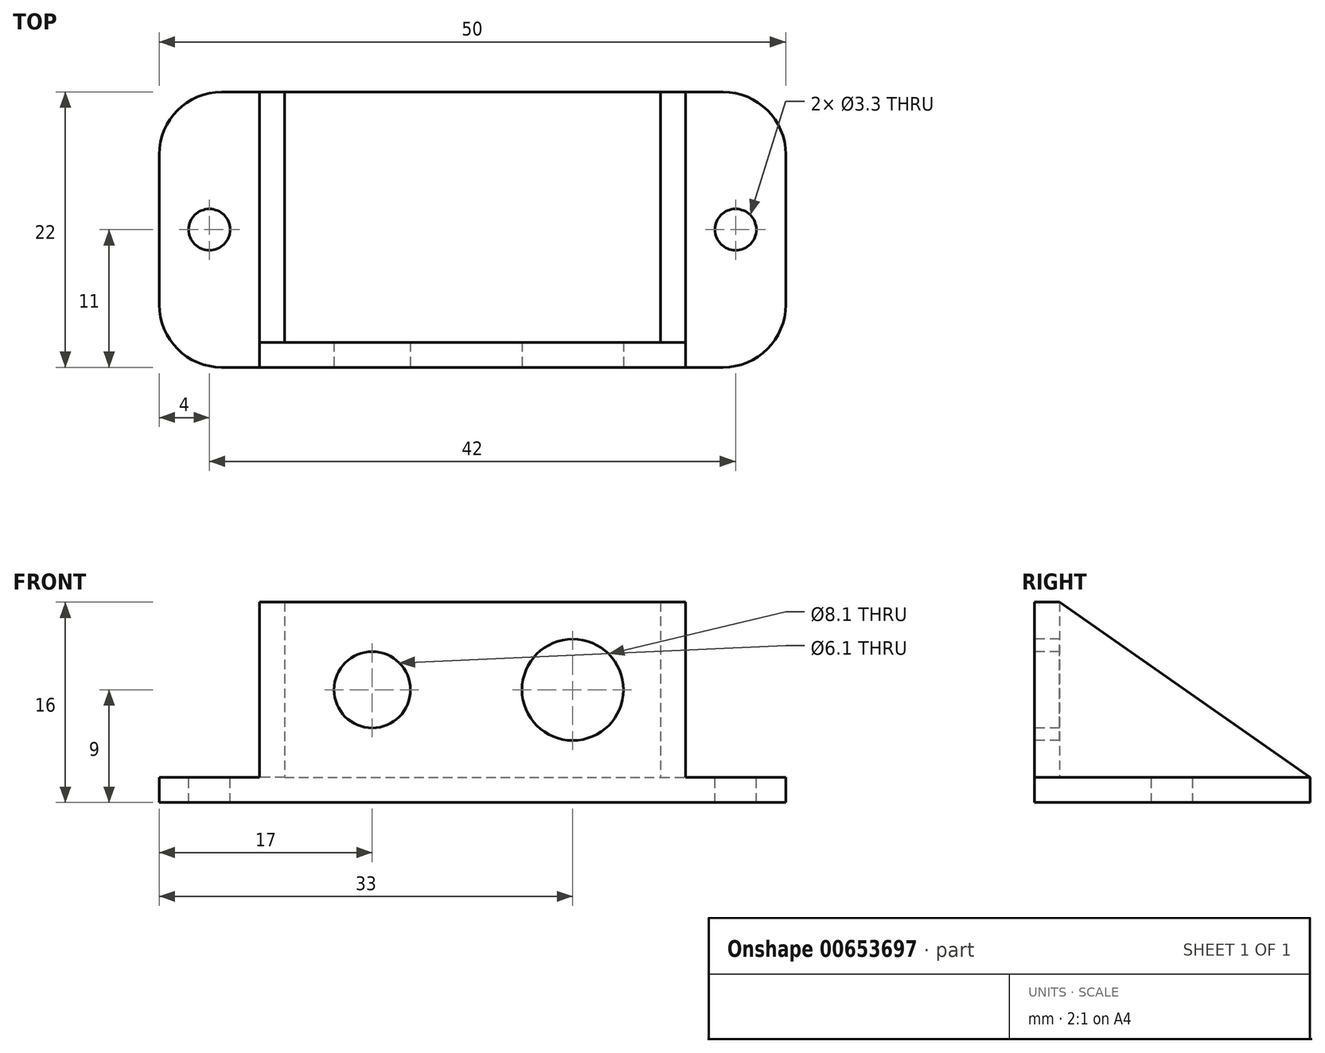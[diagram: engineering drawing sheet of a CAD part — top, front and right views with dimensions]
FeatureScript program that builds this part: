
annotation { "Feature Type Name" : "Feature", "Feature Type Description" : "" }
export const myFeature = defineFeature(function(context is Context, id is Id, definition is map)
    precondition{}
    {
        {
            var Q0;
            Q0=qCreatedBy(makeId("Top.planeOp"),FACE);
            var sketch = newSketch(context, id + "F0", { "sketchPlane" : qUnion([Q0])});
            skLineSegment(sketch, "E0.bottom", {"start": v(-25, 11) * mm, "end": v(25, 11) * mm});
            skLineSegment(sketch, "E0.top", {"start": v(-25, -11) * mm, "end": v(25, -11) * mm});
            skLineSegment(sketch, "E0.left", {"start": v(-25, 11) * mm, "end": v(-25, -11) * mm});
            skLineSegment(sketch, "E0.right", {"start": v(25, 11) * mm, "end": v(25, -11) * mm});
            skPoint(sketch, "E0.middle", {"position": v(0, 0) * mm});
            skSolve(sketch);
        }
        {
            var Q0;
            Q0=makeQuery(id+"F0.imprint","IMPRINT",FACE,{"disambiguationData":[TD([[makeQuery(id+"F0.imprint","IMPRINT",EDGE,{"derivedFrom":sQuery(id+"F0.wireOp",EDGE,"E0.bottom")}),-1.0]])]});
            extrude(context, id + "F1", {"entities" : qUnion([Q0]), "depth" : 2 * mm, "offsetDistance" : 25 * mm});
        }
        {
            var Q0;
            Q0=makeQuery(id+"F1.opExtrude","CAP_FACE",FACE,{"disambiguationData":[OSD([sQuery(id+"F0.wireOp",EDGE,"E0.bottom"),sQuery(id+"F0.wireOp",EDGE,"E0.top"),sQuery(id+"F0.wireOp",EDGE,"E0.left"),sQuery(id+"F0.wireOp",EDGE,"E0.right")])],"isStart":false});
            var sketch = newSketch(context, id + "F2", { "sketchPlane" : qUnion([Q0])});
            skLineSegment(sketch, "E1.bottom", {"start": v(17, -11) * mm, "end": v(-17, -11) * mm});
            skLineSegment(sketch, "E1.top", {"start": v(17, -9) * mm, "end": v(-17, -9) * mm});
            skLineSegment(sketch, "E1.left", {"start": v(17, -11) * mm, "end": v(17, -9) * mm});
            skLineSegment(sketch, "E1.right", {"start": v(-17, -11) * mm, "end": v(-17, -9) * mm});
            skPoint(sketch, "E1.middle", {"position": v(0, -10) * mm});
            skPoint(sketch, "E1.middle.positionSnap0", {"position": v(0, -11) * mm});
            skPoint(sketch, "E1.centerSnap0", {"position": v(0, -11) * mm});
            skSolve(sketch);
        }
        {
            var Q0;
            Q0=makeQuery(id+"F2.imprint","IMPRINT",FACE,{"disambiguationData":[TD([[makeQuery(id+"F2.imprint","IMPRINT",EDGE,{"derivedFrom":sQuery(id+"F2.wireOp",EDGE,"E1.bottom")}),1.0]])]});
            extrude(context, id + "F3", {"entities" : qUnion([Q0]), "operationType" : NewBodyOperationType.ADD, "depth" : 14 * mm, "offsetDistance" : 25 * mm});
        }
        {
            var Q0;
            Q0=makeQuery(id+"F3.boolean.opBoolean","MERGE",FACE,{"derivedFrom":[makeQuery(id+"F1.opExtrude","SWEPT_FACE",FACE,{"disambiguationData":[OSD([sQuery(id+"F0.wireOp",EDGE,"E0.top")])]}),makeQuery(id+"F3.opExtrude","SWEPT_FACE",FACE,{"disambiguationData":[OSD([sQuery(id+"F2.wireOp",EDGE,"E1.bottom")])]})]});
            var sketch = newSketch(context, id + "F4", { "sketchPlane" : qUnion([Q0])});
            skCircle(sketch, "E2", {"center": v(-8, 9) * mm, "radius": 3.05 * mm});
            skCircle(sketch, "E3", {"center": v(8, 9) * mm, "radius": 4.05 * mm});
            skSolve(sketch);
        }
        {
            var Q0;
            Q0 = qSketchRegion(id + "F4", true);
            extrude(context, id + "F5", {"entities" : qUnion([Q0]), "operationType" : NewBodyOperationType.REMOVE, "oppositeDirection" : true, "depth" : 2 * mm, "offsetDistance" : 25 * mm});
        }
        {
            var Q0;
            Q0=makeQuery(id+"F1.opExtrude","CAP_FACE",FACE,{"disambiguationData":[OSD([sQuery(id+"F0.wireOp",EDGE,"E0.bottom"),sQuery(id+"F0.wireOp",EDGE,"E0.top"),sQuery(id+"F0.wireOp",EDGE,"E0.left"),sQuery(id+"F0.wireOp",EDGE,"E0.right")])],"isStart":false});
            var sketch = newSketch(context, id + "F6", { "sketchPlane" : qUnion([Q0])});
            skCircle(sketch, "E4", {"center": v(-21, 0) * mm, "radius": 1.65 * mm});
            skCircle(sketch, "E5", {"center": v(21, 0) * mm, "radius": 1.65 * mm});
            skSolve(sketch);
        }
        {
            var Q0;
            Q0 = qSketchRegion(id + "F6", true);
            extrude(context, id + "F7", {"entities" : qUnion([Q0]), "operationType" : NewBodyOperationType.REMOVE, "oppositeDirection" : true, "depth" : 2 * mm, "offsetDistance" : 25 * mm});
        }
        {
            var Q0;
            Q0=makeQuery(id+"F3.opExtrude","SWEPT_FACE",FACE,{"disambiguationData":[OSD([sQuery(id+"F2.wireOp",EDGE,"E1.left")])]});
            var sketch = newSketch(context, id + "F8", { "sketchPlane" : qUnion([Q0])});
            skLineSegment(sketch, "E6", {"start": v(-9, 16) * mm, "end": v(11, 2) * mm});
            skLineSegment(sketch, "E7", {"start": v(11, 2) * mm, "end": v(-9, 2) * mm});
            skLineSegment(sketch, "E8", {"start": v(-9, 2) * mm, "end": v(-9, 16) * mm});
            skSolve(sketch);
        }
        {
            var Q0;
            Q0 = qSketchRegion(id + "F8", true);
            extrude(context, id + "F9", {"entities" : qUnion([Q0]), "operationType" : NewBodyOperationType.ADD, "oppositeDirection" : true, "depth" : 2 * mm, "offsetDistance" : 25 * mm});
        }
        {
            var Q0;
            Q0=makeQuery(id+"F3.opExtrude","SWEPT_FACE",FACE,{"disambiguationData":[OSD([sQuery(id+"F2.wireOp",EDGE,"E1.right")])]});
            var sketch = newSketch(context, id + "F10", { "sketchPlane" : qUnion([Q0])});
            skLineSegment(sketch, "E9", {"start": v(9, 16) * mm, "end": v(-11, 2) * mm});
            skLineSegment(sketch, "E10", {"start": v(-11, 2) * mm, "end": v(9, 2) * mm});
            skLineSegment(sketch, "E11", {"start": v(9, 2) * mm, "end": v(9, 16) * mm});
            skSolve(sketch);
        }
        {
            var Q0;
            Q0 = qSketchRegion(id + "F10", true);
            extrude(context, id + "F11", {"entities" : qUnion([Q0]), "operationType" : NewBodyOperationType.ADD, "oppositeDirection" : true, "depth" : 2 * mm, "offsetDistance" : 25 * mm});
        }
        {
            var Q0;
            Q0=makeQuery(id+"F1.opExtrude","SWEPT_EDGE",EDGE,{"disambiguationData":[OSD([sQuery(id+"F0.wireOp",EDGE,"E0.bottom"),sQuery(id+"F0.wireOp",EDGE,"E0.left")])]});
            var Q1;
            Q1=makeQuery(id+"F1.opExtrude","SWEPT_EDGE",EDGE,{"disambiguationData":[OSD([sQuery(id+"F0.wireOp",EDGE,"E0.top"),sQuery(id+"F0.wireOp",EDGE,"E0.left")])]});
            fillet(context, id + "F12", {"entities" : qUnion([Q0, Q1]), "radius" : 5 * mm, "tangentPropagation" : true, "allowEdgeOverflow" : false});
        }
        {
            var Q0;
            Q0=makeQuery(id+"F1.opExtrude","SWEPT_EDGE",EDGE,{"disambiguationData":[OSD([sQuery(id+"F0.wireOp",EDGE,"E0.top"),sQuery(id+"F0.wireOp",EDGE,"E0.right")])]});
            var Q1;
            Q1=makeQuery(id+"F1.opExtrude","SWEPT_EDGE",EDGE,{"disambiguationData":[OSD([sQuery(id+"F0.wireOp",EDGE,"E0.bottom"),sQuery(id+"F0.wireOp",EDGE,"E0.right")])]});
            fillet(context, id + "F13", {"entities" : qUnion([Q0, Q1]), "radius" : 5 * mm, "tangentPropagation" : true, "allowEdgeOverflow" : false});
        }
    });
